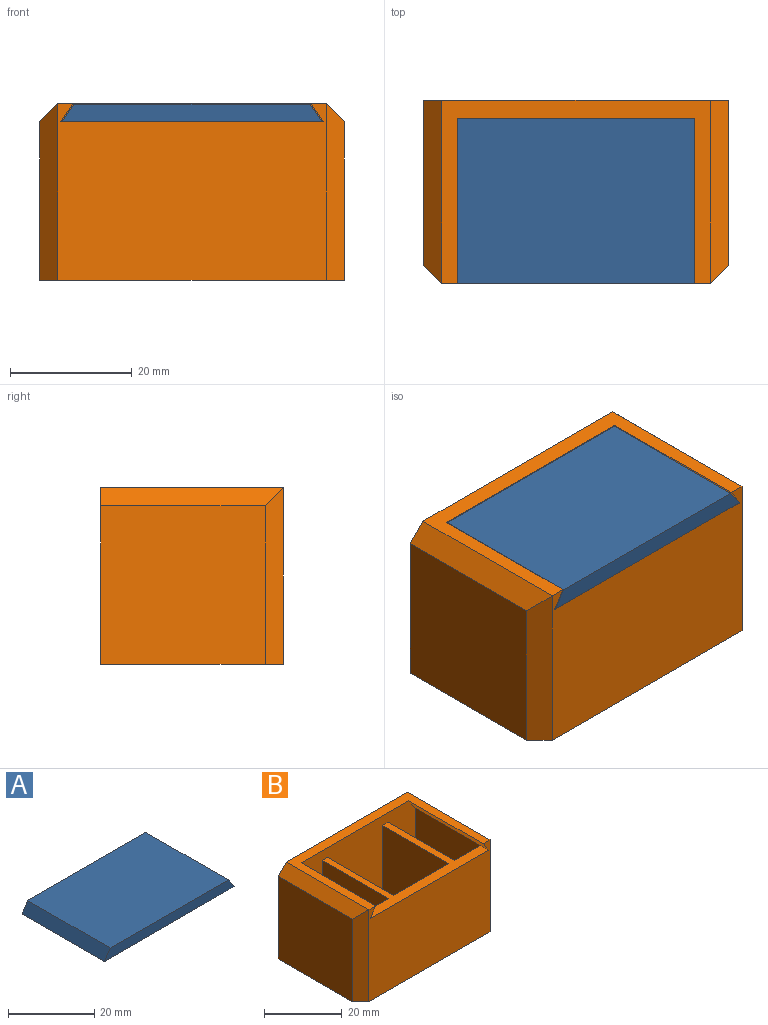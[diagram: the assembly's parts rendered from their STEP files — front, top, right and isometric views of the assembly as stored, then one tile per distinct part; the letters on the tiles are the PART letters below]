
ASSEMBLY  parts=2 mates=1
PART A: 6 faces, bbox 42.6x27x2.9 mm
  f0: plane 42.63x2.9mm, normal (0,-1,0), area 118mm2, adj f1,f2,f3,f4
  f1: plane 38.76x27mm, normal (0,0,1), area 1046.5mm2, adj f0,f2,f4,f5
  f2: plane 27x2.9mm, normal (-0.83,0,0.55), area 94.1mm2, adj f0,f1,f3,f5
  f3: plane 42.63x27mm, normal (0,0,-1), area 1150.9mm2, adj f0,f2,f4,f5
  f4: plane 27x2.9mm, normal (0.83,0,0.55), area 94.1mm2, adj f0,f1,f3,f5
  f5: plane 42.63x2.9mm, normal (0,1,0), area 118mm2, adj f1,f2,f3,f4
PART B: 28 faces, bbox 50x30x29 mm
  f0: plane 44x26mm, normal (0,-1,0), area 1043mm2, adj f1,f10,f11,f12,f13,f14,f15,f16
  f1: plane 24x23mm, normal (1,0,0), area 552mm2, adj f0,f4,f11,f23
  f2: plane 23x10mm, normal (0,1,0), area 230mm2, adj f13,f17,f18,f19,f22
  f3: plane 23x20mm, normal (0,1,0), area 460mm2, adj f13,f14,f15,f16
  f4: plane 23x10mm, normal (0,1,0), area 230mm2, adj f1,f11,f12,f13,f23
  f5: plane 44x29mm, normal (0,-1,0), area 1153mm2, adj f9,f10,f13,f20,f21,f25,f27
  f6: plane 27x26mm, normal (1,0,0), area 702mm2, adj f7,f9,f24,f25
  f7: plane 50x29mm, normal (0,1,0), area 1441mm2, adj f6,f8,f9,f10,f24,f26
  f8: plane 27x26mm, normal (-1,0,0), area 702mm2, adj f7,f9,f26,f27
  f9: plane 50x30mm, normal (0,0,-1), area 1491mm2, adj f5,f6,f7,f8,f25,f27
  f10: plane 44x30mm, normal (0,0,1), area 267mm2, adj f0,f5,f7,f20,f21,f24,f26
  f11: plane 24x10mm, normal (0,0,1), area 240mm2, adj f0,f1,f4,f12
  f12: plane 24x23mm, normal (-1,0,0), area 552mm2, adj f0,f4,f11,f13
  f13: plane 43x27mm, normal (0,0,1), area 225mm2, adj f0,f2,f3,f4,f5,f12,f14,f16
  f14: plane 24x23mm, normal (1,0,0), area 552mm2, adj f0,f3,f13,f15
  f15: plane 24x20mm, normal (0,0,1), area 480mm2, adj f0,f3,f14,f16
  f16: plane 24x23mm, normal (-1,0,0), area 552mm2, adj f0,f3,f13,f15
  f17: plane 24x23mm, normal (1,0,0), area 552mm2, adj f0,f2,f13,f18
  f18: plane 24x10mm, normal (0,0,1), area 240mm2, adj f0,f2,f17,f19
  f19: plane 24x23mm, normal (-1,0,0), area 552mm2, adj f0,f2,f18,f22
  f20: plane 27x3mm, normal (0.83,0,-0.55), area 97.3mm2, adj f0,f5,f10,f13,f23
  f21: plane 27x3mm, normal (-0.83,0,-0.55), area 97.3mm2, adj f0,f5,f10,f13,f22
  f22: plane 24x0.5mm, normal (0,0,-1), area 12mm2, adj f0,f2,f19,f21
  f23: plane 24x0.5mm, normal (0,0,-1), area 12mm2, adj f0,f1,f4,f20
  f24: plane 30x3mm, normal (0.71,0,0.71), area 120.9mm2, adj f6,f7,f10,f25
  f25: plane 29x3mm, normal (0.71,-0.71,0), area 116.7mm2, adj f5,f6,f9,f24
  f26: plane 30x3mm, normal (-0.71,0,0.71), area 120.9mm2, adj f7,f8,f10,f27
  f27: plane 29x3mm, normal (-0.71,-0.71,0), area 116.7mm2, adj f5,f8,f9,f26
PLACE A t=(-0.72,2.26,-10.59)mm
PLACE B t=(-0.72,2.26,-10.49)mm
MATE slider A.f0 <-> B.f5  axis (0,-1,0) through (-0.72,-12.74,15.51)mm
